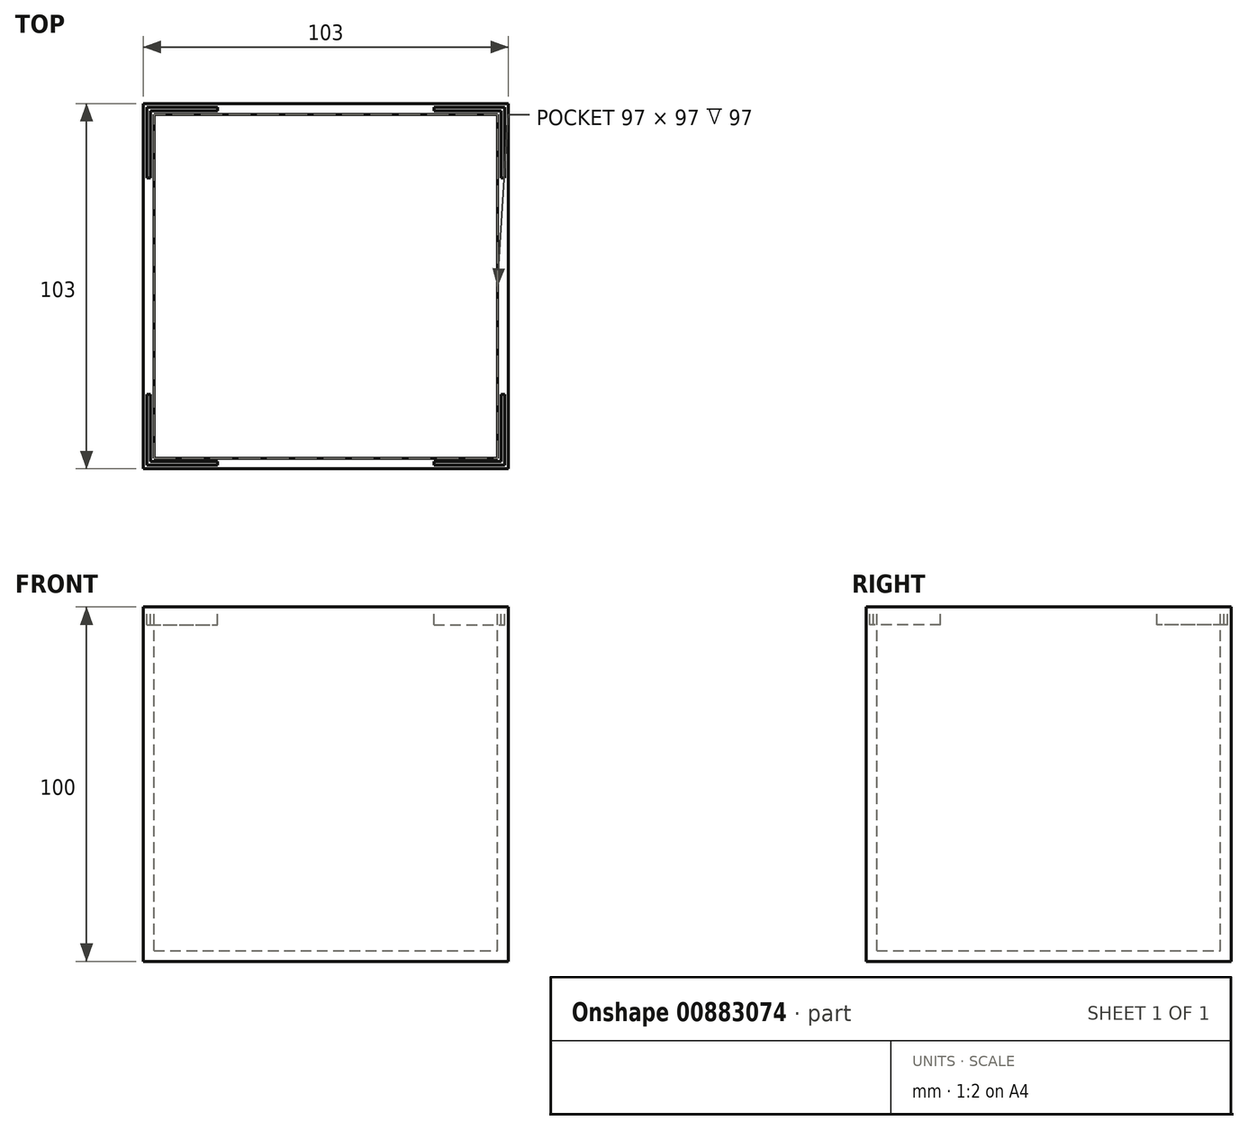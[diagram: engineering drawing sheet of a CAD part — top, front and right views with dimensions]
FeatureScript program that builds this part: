
annotation { "Feature Type Name" : "Feature", "Feature Type Description" : "" }
export const myFeature = defineFeature(function(context is Context, id is Id, definition is map)
    precondition{}
    {
        {
            var Q0;
            Q0=qCreatedBy(makeId("Top.planeOp"),FACE);
            var sketch = newSketch(context, id + "F0", { "sketchPlane" : qUnion([Q0])});
            skLineSegment(sketch, "E0.bottom", {"start": v(0, 0) * mm, "end": v(103, 0) * mm});
            skLineSegment(sketch, "E0.top", {"start": v(0, 103) * mm, "end": v(103, 103) * mm});
            skLineSegment(sketch, "E0.left", {"start": v(0, 0) * mm, "end": v(0, 103) * mm});
            skLineSegment(sketch, "E0.right", {"start": v(103, 0) * mm, "end": v(103, 103) * mm});
            skSolve(sketch);
        }
        {
            var Q0;
            Q0 = qSketchRegion(id + "F0", true);
            var Q1;
            Q1=makeQuery(id+"F0.imprint","IMPRINT",FACE,{"disambiguationData":[TD([[makeQuery(id+"F0.imprint","IMPRINT",EDGE,{"derivedFrom":sQuery(id+"F0.wireOp",EDGE,"E0.bottom")}),1.0]])]});
            extrude(context, id + "F1", {"entities" : qUnion([Q0, Q1]), "depth" : 100 * mm, "offsetDistance" : 25 * mm});
        }
        {
            var Q0;
            Q0=makeQuery(id+"F1.opExtrude","CAP_FACE",FACE,{"disambiguationData":[OSD([sQuery(id+"F0.wireOp",EDGE,"E0.bottom"),sQuery(id+"F0.wireOp",EDGE,"E0.top"),sQuery(id+"F0.wireOp",EDGE,"E0.left"),sQuery(id+"F0.wireOp",EDGE,"E0.right")])],"isStart":false});
            var sketch = newSketch(context, id + "F2", { "sketchPlane" : qUnion([Q0])});
            skLineSegment(sketch, "E1.0", {"start": v(3, 100) * mm, "end": v(100, 100) * mm});
            skLineSegment(sketch, "E1.1", {"start": v(3, 3) * mm, "end": v(3, 100) * mm});
            skLineSegment(sketch, "E1.2", {"start": v(3, 3) * mm, "end": v(100, 3) * mm});
            skLineSegment(sketch, "E1.3", {"start": v(100, 3) * mm, "end": v(100, 100) * mm});
            skSolve(sketch);
        }
        {
            var Q0;
            Q0=makeQuery(id+"F2.imprint","IMPRINT",FACE,{"disambiguationData":[TD([[makeQuery(id+"F2.imprint","IMPRINT",EDGE,{"derivedFrom":sQuery(id+"F2.wireOp",EDGE,"E1.0")}),-1.0]])]});
            extrude(context, id + "F3", {"entities" : qUnion([Q0]), "operationType" : NewBodyOperationType.REMOVE, "oppositeDirection" : true, "depth" : 97 * mm, "offsetDistance" : 25 * mm});
        }
        {
            var Q0;
            Q0=makeQuery(id+"F1.opExtrude","CAP_FACE",FACE,{"disambiguationData":[OSD([sQuery(id+"F0.wireOp",EDGE,"E0.bottom"),sQuery(id+"F0.wireOp",EDGE,"E0.top"),sQuery(id+"F0.wireOp",EDGE,"E0.left"),sQuery(id+"F0.wireOp",EDGE,"E0.right")])],"isStart":false});
            var sketch = newSketch(context, id + "F4", { "sketchPlane" : qUnion([Q0])});
            skLineSegment(sketch, "E2.bottom", {"start": v(1, 102) * mm, "end": v(21, 102) * mm});
            skLineSegment(sketch, "E2.top", {"start": v(1, 101) * mm, "end": v(21, 101) * mm});
            skLineSegment(sketch, "E2.left", {"start": v(1, 102) * mm, "end": v(1, 101) * mm});
            skLineSegment(sketch, "E2.right", {"start": v(21, 102) * mm, "end": v(21, 101) * mm});
            skLineSegment(sketch, "E3.bottom", {"start": v(1, 101) * mm, "end": v(2, 101) * mm});
            skLineSegment(sketch, "E3.top", {"start": v(1, 82) * mm, "end": v(2, 82) * mm});
            skLineSegment(sketch, "E3.left", {"start": v(1, 101) * mm, "end": v(1, 82) * mm});
            skLineSegment(sketch, "E3.right", {"start": v(2, 101) * mm, "end": v(2, 82) * mm});
            skLineSegment(sketch, "E4.bottom", {"start": v(1, 21) * mm, "end": v(2, 21) * mm});
            skLineSegment(sketch, "E4.top", {"start": v(1, 1) * mm, "end": v(2, 1) * mm});
            skLineSegment(sketch, "E4.left", {"start": v(1, 21) * mm, "end": v(1, 1) * mm});
            skLineSegment(sketch, "E4.right", {"start": v(2, 21) * mm, "end": v(2, 1) * mm});
            skLineSegment(sketch, "E5.bottom", {"start": v(2, 2) * mm, "end": v(21, 2) * mm});
            skLineSegment(sketch, "E5.top", {"start": v(2, 1) * mm, "end": v(21, 1) * mm});
            skLineSegment(sketch, "E5.left", {"start": v(2, 2) * mm, "end": v(2, 1) * mm});
            skLineSegment(sketch, "E5.right", {"start": v(21, 2) * mm, "end": v(21, 1) * mm});
            skLineSegment(sketch, "E6.bottom", {"start": v(82, 2) * mm, "end": v(102, 2) * mm});
            skLineSegment(sketch, "E6.top", {"start": v(82, 1) * mm, "end": v(102, 1) * mm});
            skLineSegment(sketch, "E6.left", {"start": v(82, 2) * mm, "end": v(82, 1) * mm});
            skLineSegment(sketch, "E6.right", {"start": v(102, 2) * mm, "end": v(102, 1) * mm});
            skLineSegment(sketch, "E7.bottom", {"start": v(101, 2) * mm, "end": v(102, 2) * mm});
            skLineSegment(sketch, "E7.top", {"start": v(101, 21) * mm, "end": v(102, 21) * mm});
            skLineSegment(sketch, "E7.left", {"start": v(101, 2) * mm, "end": v(101, 21) * mm});
            skLineSegment(sketch, "E7.right", {"start": v(102, 2) * mm, "end": v(102, 21) * mm});
            skLineSegment(sketch, "E8.bottom", {"start": v(82, 102) * mm, "end": v(102, 102) * mm});
            skLineSegment(sketch, "E8.top", {"start": v(82, 101) * mm, "end": v(102, 101) * mm});
            skLineSegment(sketch, "E8.left", {"start": v(82, 102) * mm, "end": v(82, 101) * mm});
            skLineSegment(sketch, "E8.right", {"start": v(102, 102) * mm, "end": v(102, 101) * mm});
            skLineSegment(sketch, "E9.bottom", {"start": v(101, 101) * mm, "end": v(102, 101) * mm});
            skLineSegment(sketch, "E9.top", {"start": v(101, 82) * mm, "end": v(102, 82) * mm});
            skLineSegment(sketch, "E9.left", {"start": v(101, 101) * mm, "end": v(101, 82) * mm});
            skLineSegment(sketch, "E9.right", {"start": v(102, 101) * mm, "end": v(102, 82) * mm});
            skSolve(sketch);
        }
        {
            var Q0;
            Q0 = qSketchRegion(id + "F4", true);
            var Q1;
            Q1=makeQuery(id+"F4.imprint","IMPRINT",FACE,{"disambiguationData":[TD([[makeQuery(id+"F4.imprint","IMPRINT",EDGE,{"derivedFrom":sQuery(id+"F4.wireOp",EDGE,"E8.bottom")}),-1.0]])]});
            extrude(context, id + "F5", {"entities" : qUnion([Q0, Q1]), "operationType" : NewBodyOperationType.REMOVE, "oppositeDirection" : true, "depth" : 5 * mm, "offsetDistance" : 25 * mm});
        }
    });
